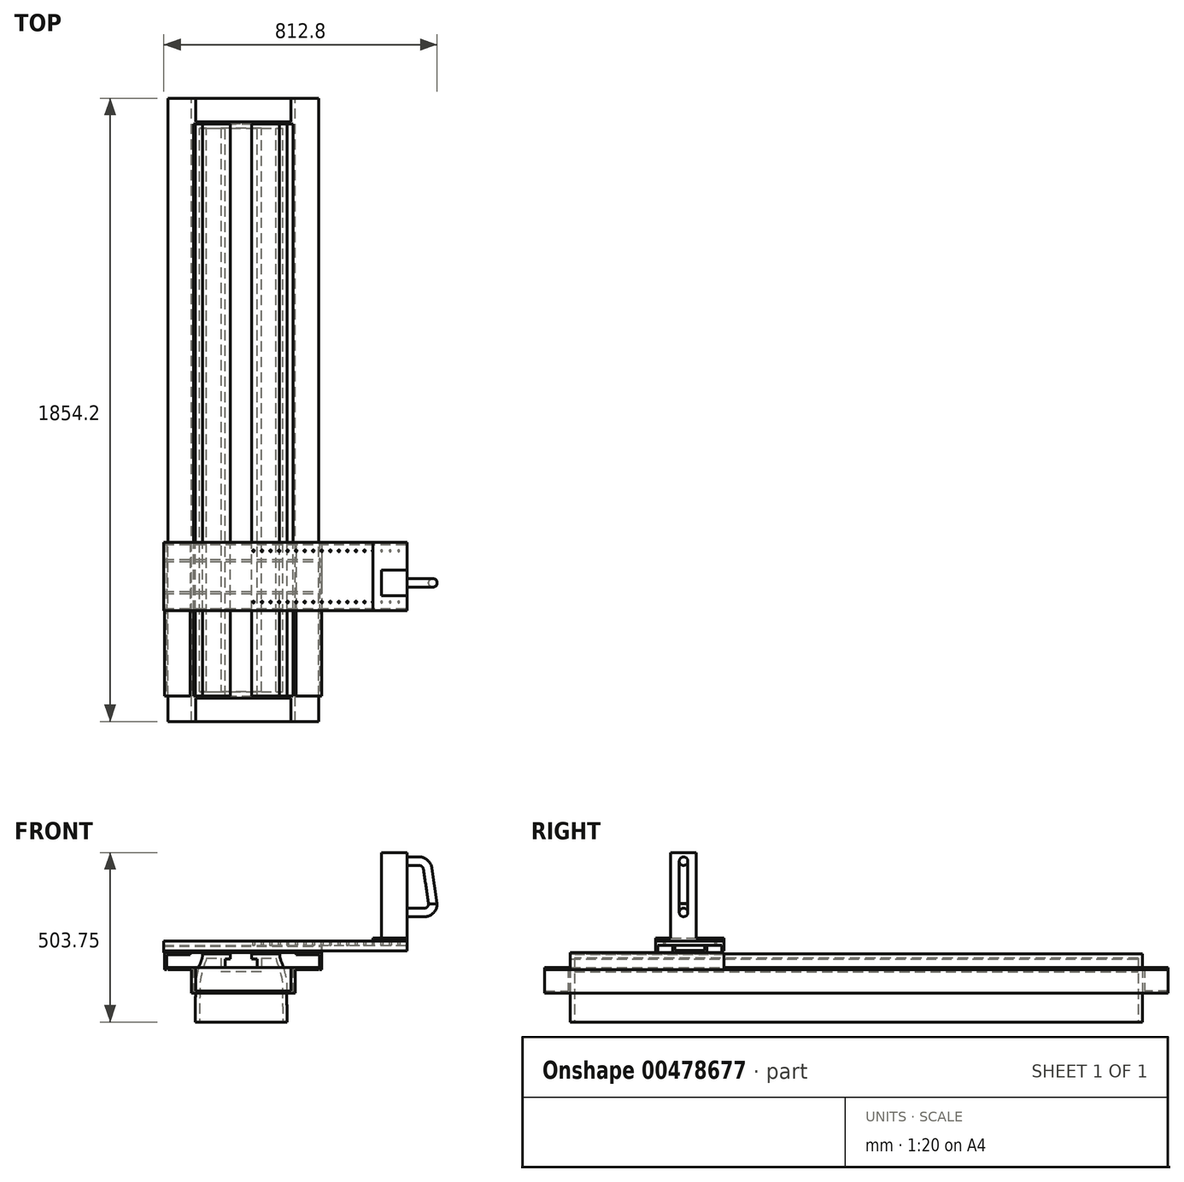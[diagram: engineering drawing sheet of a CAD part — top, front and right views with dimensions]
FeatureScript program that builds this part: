
annotation { "Feature Type Name" : "Feature", "Feature Type Description" : "" }
export const myFeature = defineFeature(function(context is Context, id is Id, definition is map)
    precondition{}
    {
        {
            var Q0;
            Q0=qCreatedBy(makeId("Front.planeOp"),FACE);
            var sketch = newSketch(context, id + "F0", { "sketchPlane" : qUnion([Q0])});
            skLineSegment(sketch, "E0.bottom", {"start": v(0, 0) * mm, "end": v(136.53, 0) * mm});
            skLineSegment(sketch, "E0.top", {"start": v(22.23, 203.2) * mm, "end": v(104.78, 203.2) * mm});
            skLineSegment(sketch, "E1.left", {"start": v(-15.88, 0) * mm, "end": v(-15.88, 203.2) * mm, "construction": true});
            skPoint(sketch, "E2", {"position": v(22.23, 203.2) * mm});
            skPoint(sketch, "E3", {"position": v(20.52, 190.5) * mm});
            skPoint(sketch, "E4", {"position": v(16.18, 177.8) * mm});
            skPoint(sketch, "E5", {"position": v(11.43, 165.1) * mm});
            skPoint(sketch, "E6", {"position": v(8.2, 152.4) * mm});
            skPoint(sketch, "E7", {"position": v(4.98, 139.7) * mm});
            skPoint(sketch, "E8", {"position": v(2.49, 127) * mm});
            skPoint(sketch, "E9", {"position": v(1.37, 114.3) * mm});
            skPoint(sketch, "E10", {"position": v(1.07, 101.6) * mm});
            skFitSpline(sketch, "E11", {"points": [v(22.23, 203.2) * mm, v(20.52, 190.5) * mm, v(16.18, 177.8) * mm, v(11.43, 165.1) * mm, v(8.2, 152.4) * mm, v(4.98, 139.7) * mm, v(2.49, 127) * mm, v(1.37, 114.3) * mm, v(1.07, 101.6) * mm, v(0, 0) * mm], "startDerivative": vector(-11.78, -139.04) * mm, "endDerivative": vector(-5, -490.08) * mm});
            skPoint(sketch, "E12", {"position": v(136.53, 0) * mm});
            skLineSegment(sketch, "E13", {"start": v(136.52, 203.2) * mm, "end": v(136.52, 0) * mm, "construction": true});
            skFitSpline(sketch, "E14.MirrorCS", {"points": [v(250.82, 203.2) * mm, v(252.53, 190.5) * mm, v(256.87, 177.8) * mm, v(261.62, 165.1) * mm, v(264.86, 152.4) * mm, v(268.07, 139.7) * mm, v(270.56, 127) * mm, v(271.68, 114.3) * mm, v(271.98, 101.6) * mm, v(273.05, 0) * mm], "startDerivative": vector(11.78, -139.04) * mm, "endDerivative": vector(5, -490.08) * mm});
            skLineSegment(sketch, "E15.MirrorCS", {"start": v(273.05, 0) * mm, "end": v(136.53, 0) * mm});
            skPoint(sketch, "E16.middle", {"position": v(136.52, 203.2) * mm});
            skLineSegment(sketch, "E17", {"start": v(104.78, 203.2) * mm, "end": v(104.78, 187.33) * mm});
            skLineSegment(sketch, "E18", {"start": v(104.78, 187.33) * mm, "end": v(88.9, 187.33) * mm});
            skLineSegment(sketch, "E19", {"start": v(88.9, 187.33) * mm, "end": v(88.9, 161.93) * mm});
            skLineSegment(sketch, "E20", {"start": v(88.9, 161.93) * mm, "end": v(136.52, 161.93) * mm});
            skLineSegment(sketch, "E21.MirrorCS", {"start": v(184.15, 187.33) * mm, "end": v(184.15, 161.93) * mm});
            skLineSegment(sketch, "E22.MirrorCS", {"start": v(184.15, 161.93) * mm, "end": v(136.53, 161.93) * mm});
            skLineSegment(sketch, "E23.MirrorCS", {"start": v(168.28, 187.33) * mm, "end": v(184.15, 187.33) * mm});
            skLineSegment(sketch, "E24.MirrorCS", {"start": v(168.28, 203.2) * mm, "end": v(168.28, 187.33) * mm});
            skPoint(sketch, "E25", {"position": v(104.78, 203.2) * mm});
            skPoint(sketch, "E26", {"position": v(168.28, 203.2) * mm});
            skLineSegment(sketch, "E27", {"start": v(168.28, 203.2) * mm, "end": v(250.83, 203.2) * mm});
            skLineSegment(sketch, "E28", {"start": v(0, 0) * mm, "end": v(2.5, 237.7) * mm, "construction": true});
            skSolve(sketch);
        }
        {
            var Q0;
            Q0=makeQuery(id+"F0.imprint","IMPRINT",FACE,{"disambiguationData":[TD([[makeQuery(id+"F0.imprint","IMPRINT",EDGE,{"derivedFrom":sQuery(id+"F0.wireOp",EDGE,"E0.bottom")}),1.0]])]});
            extrude(context, id + "F1", {"entities" : qUnion([Q0]), "depth" : 1701.8 * mm, "offsetDistance" : 25.4 * mm});
        }
        {
            var Q0;
            Q0=makeQuery(id+"F1.opExtrude","SWEPT_FACE",FACE,{"disambiguationData":[OSD([sQuery(id+"F0.wireOp",EDGE,"E0.bottom"),sQuery(id+"F0.wireOp",EDGE,"E15.MirrorCS")])]});
            shell(context, id + "F2", {"entities" : qUnion([Q0]), "thickness" : 12.7 * mm});
        }
        {
            var Q0;
            Q0=makeQuery(id+"F1.opExtrude","CAP_FACE",FACE,{"disambiguationData":[OSD([sQuery(id+"F0.wireOp",EDGE,"E0.bottom"),sQuery(id+"F0.wireOp",EDGE,"E0.top"),sQuery(id+"F0.wireOp",EDGE,"E11"),sQuery(id+"F0.wireOp",EDGE,"E14.MirrorCS"),sQuery(id+"F0.wireOp",EDGE,"E15.MirrorCS"),sQuery(id+"F0.wireOp",EDGE,"E17"),sQuery(id+"F0.wireOp",EDGE,"E18"),sQuery(id+"F0.wireOp",EDGE,"E19"),sQuery(id+"F0.wireOp",EDGE,"E20"),sQuery(id+"F0.wireOp",EDGE,"E21.MirrorCS"),sQuery(id+"F0.wireOp",EDGE,"E22.MirrorCS"),sQuery(id+"F0.wireOp",EDGE,"E23.MirrorCS"),sQuery(id+"F0.wireOp",EDGE,"E24.MirrorCS"),sQuery(id+"F0.wireOp",EDGE,"E27")])],"isStart":true});
            var sketch = newSketch(context, id + "F3", { "sketchPlane" : qUnion([Q0])});
            skLineSegment(sketch, "E29.bottom", {"start": v(-290.95, 85.73) * mm, "end": v(5.4, 85.73) * mm});
            skPoint(sketch, "E29.middle", {"position": v(-136.52, 123.83) * mm});
            skLineSegment(sketch, "E30", {"start": v(-284.6, 92.08) * mm, "end": v(-0.95, 92.08) * mm});
            skLineSegment(sketch, "E31", {"start": v(5.4, 161.93) * mm, "end": v(5.4, 85.73) * mm});
            skLineSegment(sketch, "E32.trimOffspring", {"start": v(-290.95, 161.92) * mm, "end": v(5.4, 161.93) * mm});
            skLineSegment(sketch, "E33", {"start": v(-290.95, 161.92) * mm, "end": v(-290.95, 85.73) * mm});
            skLineSegment(sketch, "E34", {"start": v(-0.95, 92.08) * mm, "end": v(-0.95, 161.93) * mm});
            skPoint(sketch, "E35.orphan", {"position": v(-0.95, 85.73) * mm});
            skLineSegment(sketch, "E36", {"start": v(-284.6, 161.92) * mm, "end": v(-284.6, 92.08) * mm});
            skSolve(sketch);
        }
        {
            var Q0;
            Q0 = qSketchRegion(id + "F3", true);
            extrude(context, id + "F4", {"entities" : qUnion([Q0]), "depth" : 6.35 * mm, "offsetDistance" : 25.4 * mm});
        }
        {
            var Q0;
            {var subQ4=sQuery(id+"F3.wireOp",EDGE,"E29.left");Q0=makeQuery(id+"F3.imprint","IMPRINT",FACE,{"disambiguationData":[TD([[makeQuery(id+"F3.imprint","IMPRINT",EDGE,{"derivedFrom":subQ4}),-1.0]])]});}
            var Q1;
            {var subQ0=sQuery(id+"F3.wireOp",EDGE,"E29.bottom");var subQ1=makeQuery(id+"F1.opExtrude","CAP_EDGE",EDGE,{"disambiguationData":[OSD([sQuery(id+"F0.wireOp",EDGE,"E14.MirrorCS")])],"isStart":true});var subQ2=makeQuery(id+"F3.imprint","INTERSECT",VERTEX,{"derivedFrom":[subQ1,subQ0]});Q1=makeQuery(id+"F3.imprint","IMPRINT",FACE,{"disambiguationData":[TD([[makeQuery(id+"F3.imprint","IMPRINT",EDGE,{"disambiguationData":[TD([[subQ2,-1.0]])],"derivedFrom":subQ0}),1.0]])]});}
            var Q2;
            {var subQ4=sQuery(id+"F3.wireOp",EDGE,"E29.right");Q2=makeQuery(id+"F3.imprint","IMPRINT",FACE,{"disambiguationData":[TD([[makeQuery(id+"F3.imprint","IMPRINT",EDGE,{"derivedFrom":subQ4}),1.0]])]});}
            extrude(context, id + "F5", {"entities" : qUnion([Q0, Q1, Q2]), "operationType" : NewBodyOperationType.ADD, "depth" : 76.2 * mm, "offsetDistance" : 25.4 * mm});
        }
        {
            var Q0;
            Q0=makeQuery(id+"F5.opExtrude","CAP_FACE",FACE,{"disambiguationData":[OSD([sQuery(id+"F3.wireOp",EDGE,"E29.bottom"),sQuery(id+"F3.wireOp",EDGE,"E29.left"),sQuery(id+"F3.wireOp",EDGE,"E29.right"),sQuery(id+"F3.wireOp",EDGE,"E30")])],"isStart":false});
            var sketch = newSketch(context, id + "F6", { "sketchPlane" : qUnion([Q0])});
            skLineSegment(sketch, "E37", {"start": v(-367.15, 161.92) * mm, "end": v(-290.95, 161.92) * mm});
            skLineSegment(sketch, "E38", {"start": v(-290.95, 161.92) * mm, "end": v(-290.95, 85.72) * mm});
            skLineSegment(sketch, "E39", {"start": v(-290.95, 85.72) * mm, "end": v(-297.3, 85.72) * mm});
            skLineSegment(sketch, "E40", {"start": v(-297.3, 85.72) * mm, "end": v(-297.3, 155.57) * mm});
            skLineSegment(sketch, "E41", {"start": v(-297.3, 155.57) * mm, "end": v(-367.15, 155.57) * mm});
            skLineSegment(sketch, "E42", {"start": v(-367.15, 155.57) * mm, "end": v(-367.15, 161.92) * mm});
            skLineSegment(sketch, "E43", {"start": v(5.4, 85.73) * mm, "end": v(5.4, 161.93) * mm});
            skLineSegment(sketch, "E44", {"start": v(5.4, 161.93) * mm, "end": v(81.6, 161.93) * mm});
            skLineSegment(sketch, "E45", {"start": v(81.6, 161.93) * mm, "end": v(81.6, 155.58) * mm});
            skLineSegment(sketch, "E46", {"start": v(81.6, 155.58) * mm, "end": v(11.75, 155.58) * mm});
            skLineSegment(sketch, "E47", {"start": v(11.75, 155.58) * mm, "end": v(11.75, 85.73) * mm});
            skLineSegment(sketch, "E48", {"start": v(11.75, 85.73) * mm, "end": v(5.4, 85.73) * mm});
            skSolve(sketch);
        }
        {
            var Q0;
            Q0 = qSketchRegion(id + "F6", true);
            extrude(context, id + "F7", {"entities" : qUnion([Q0]), "oppositeDirection" : true, "depth" : 1854.2 * mm, "offsetDistance" : 25.4 * mm});
        }
        {
            var Q0;
            {var subQ0=sQuery(id+"F3.wireOp",EDGE,"E33");Q0=makeQuery(id+"F3.imprint","IMPRINT",FACE,{"disambiguationData":[TD([[makeQuery(id+"F3.imprint","IMPRINT",EDGE,{"derivedFrom":subQ0}),1.0]])]});}
            var Q1;
            {var subQ0=sQuery(id+"F3.wireOp",EDGE,"E31");Q1=makeQuery(id+"F3.imprint","IMPRINT",FACE,{"disambiguationData":[TD([[makeQuery(id+"F3.imprint","IMPRINT",EDGE,{"derivedFrom":subQ0}),-1.0]])]});}
            extrude(context, id + "F8", {"entities" : qUnion([Q0, Q1]), "operationType" : NewBodyOperationType.ADD, "depth" : 76.2 * mm, "offsetDistance" : 25.4 * mm});
        }
        {
            var Q0;
            Q0=makeQuery(id+"F1.opExtrude","CAP_FACE",FACE,{"disambiguationData":[OSD([sQuery(id+"F0.wireOp",EDGE,"E0.bottom"),sQuery(id+"F0.wireOp",EDGE,"E0.top"),sQuery(id+"F0.wireOp",EDGE,"E11"),sQuery(id+"F0.wireOp",EDGE,"E14.MirrorCS"),sQuery(id+"F0.wireOp",EDGE,"E15.MirrorCS"),sQuery(id+"F0.wireOp",EDGE,"E17"),sQuery(id+"F0.wireOp",EDGE,"E18"),sQuery(id+"F0.wireOp",EDGE,"E19"),sQuery(id+"F0.wireOp",EDGE,"E20"),sQuery(id+"F0.wireOp",EDGE,"E21.MirrorCS"),sQuery(id+"F0.wireOp",EDGE,"E22.MirrorCS"),sQuery(id+"F0.wireOp",EDGE,"E23.MirrorCS"),sQuery(id+"F0.wireOp",EDGE,"E24.MirrorCS"),sQuery(id+"F0.wireOp",EDGE,"E27")])],"isStart":false});
            var sketch = newSketch(context, id + "F9", { "sketchPlane" : qUnion([Q0])});
            skLineSegment(sketch, "E49.bottom", {"start": v(-5.4, 85.73) * mm, "end": v(290.95, 85.73) * mm});
            skLineSegment(sketch, "E49.top", {"start": v(-5.4, 161.92) * mm, "end": v(290.95, 161.92) * mm});
            skLineSegment(sketch, "E49.left", {"start": v(-5.4, 85.33) * mm, "end": v(-5.4, 91.68) * mm});
            skLineSegment(sketch, "E49.right", {"start": v(290.95, 85.33) * mm, "end": v(290.95, 91.68) * mm});
            skLineSegment(sketch, "E50", {"start": v(-5.4, 161.92) * mm, "end": v(-5.4, 91.68) * mm});
            skLineSegment(sketch, "E51", {"start": v(290.95, 161.92) * mm, "end": v(290.95, 91.68) * mm});
            skLineSegment(sketch, "E52", {"start": v(0.95, 92.08) * mm, "end": v(284.6, 92.08) * mm});
            skLineSegment(sketch, "E53", {"start": v(0.95, 161.92) * mm, "end": v(0.95, 92.08) * mm});
            skLineSegment(sketch, "E54", {"start": v(284.6, 161.92) * mm, "end": v(284.6, 92.08) * mm});
            skSolve(sketch);
        }
        {
            var Q0;
            {var subQ0=sQuery(id+"F9.wireOp",EDGE,"E49.top");var subQ1=makeQuery(id+"F1.opExtrude","CAP_EDGE",EDGE,{"disambiguationData":[OSD([sQuery(id+"F0.wireOp",EDGE,"E11")])],"isStart":false});var subQ2=makeQuery(id+"F9.imprint","INTERSECT",VERTEX,{"derivedFrom":[subQ1,subQ0]});Q0=makeQuery(id+"F9.imprint","IMPRINT",FACE,{"disambiguationData":[TD([[makeQuery(id+"F9.imprint","IMPRINT",EDGE,{"disambiguationData":[TD([[subQ2,-1.0]])],"derivedFrom":subQ0}),-1.0]])]});}
            var Q1;
            {var subQ0=sQuery(id+"F9.wireOp",EDGE,"E54");Q1=makeQuery(id+"F9.imprint","IMPRINT",FACE,{"disambiguationData":[TD([[makeQuery(id+"F9.imprint","IMPRINT",EDGE,{"derivedFrom":subQ0}),-1.0]])]});}
            var Q2;
            {var subQ0=sQuery(id+"F9.wireOp",EDGE,"E53");Q2=makeQuery(id+"F9.imprint","IMPRINT",FACE,{"disambiguationData":[TD([[makeQuery(id+"F9.imprint","IMPRINT",EDGE,{"derivedFrom":subQ0}),1.0]])]});}
            extrude(context, id + "F10", {"entities" : qUnion([Q0, Q1, Q2]), "depth" : 6.35 * mm, "offsetDistance" : 25.4 * mm});
        }
        {
            var Q0;
            {var subQ5=sQuery(id+"F9.wireOp",EDGE,"E49.right");Q0=makeQuery(id+"F9.imprint","IMPRINT",FACE,{"disambiguationData":[TD([[makeQuery(id+"F9.imprint","IMPRINT",EDGE,{"derivedFrom":subQ5}),1.0]])]});}
            var Q1;
            {var subQ0=sQuery(id+"F9.wireOp",EDGE,"E49.bottom");var subQ1=makeQuery(id+"F1.opExtrude","CAP_EDGE",EDGE,{"disambiguationData":[OSD([sQuery(id+"F0.wireOp",EDGE,"E11")])],"isStart":false});var subQ2=makeQuery(id+"F9.imprint","INTERSECT",VERTEX,{"derivedFrom":[subQ1,subQ0]});Q1=makeQuery(id+"F9.imprint","IMPRINT",FACE,{"disambiguationData":[TD([[makeQuery(id+"F9.imprint","IMPRINT",EDGE,{"disambiguationData":[TD([[subQ2,-1.0]])],"derivedFrom":subQ0}),1.0]])]});}
            var Q2;
            {var subQ0=sQuery(id+"F9.wireOp",EDGE,"E51");Q2=makeQuery(id+"F9.imprint","IMPRINT",FACE,{"disambiguationData":[TD([[makeQuery(id+"F9.imprint","IMPRINT",EDGE,{"derivedFrom":subQ0}),-1.0]])]});}
            var Q3;
            {var subQ0=sQuery(id+"F9.wireOp",EDGE,"E50");Q3=makeQuery(id+"F9.imprint","IMPRINT",FACE,{"disambiguationData":[TD([[makeQuery(id+"F9.imprint","IMPRINT",EDGE,{"derivedFrom":subQ0}),1.0]])]});}
            extrude(context, id + "F11", {"entities" : qUnion([Q0, Q1, Q2, Q3]), "operationType" : NewBodyOperationType.ADD, "depth" : 76.2 * mm, "offsetDistance" : 25.4 * mm});
        }
        {
            var Q0;
            {var subQ0=makeQuery(id+"F1.opExtrude","CAP_EDGE",EDGE,{"disambiguationData":[OSD([sQuery(id+"F0.wireOp",EDGE,"E0.top")])],"isStart":false});Q0=makeQuery(id+"F9.imprint","IMPRINT",FACE,{"disambiguationData":[TD([[makeQuery(id+"F9.imprint","IMPRINT",EDGE,{"derivedFrom":subQ0}),-1.0]])]});}
            var sketch = newSketch(context, id + "F12", { "sketchPlane" : qUnion([Q0])});
            skLineSegment(sketch, "E55", {"start": v(-91.12, 155.57) * mm, "end": v(-91.12, 206.37) * mm});
            skLineSegment(sketch, "E56", {"start": v(-91.12, 206.37) * mm, "end": v(-14.92, 206.37) * mm});
            skLineSegment(sketch, "E57", {"start": v(-14.92, 206.37) * mm, "end": v(-14.92, 200.02) * mm});
            skLineSegment(sketch, "E58", {"start": v(-14.92, 200.02) * mm, "end": v(-84.77, 200.02) * mm});
            skLineSegment(sketch, "E59", {"start": v(-84.77, 200.02) * mm, "end": v(-84.77, 155.57) * mm});
            skLineSegment(sketch, "E60", {"start": v(-84.77, 155.57) * mm, "end": v(-91.12, 155.57) * mm});
            skLineSegment(sketch, "E61", {"start": v(300.48, 206.37) * mm, "end": v(376.68, 206.37) * mm});
            skLineSegment(sketch, "E62", {"start": v(376.68, 206.37) * mm, "end": v(376.68, 155.57) * mm});
            skLineSegment(sketch, "E63", {"start": v(376.68, 155.57) * mm, "end": v(370.33, 155.57) * mm});
            skLineSegment(sketch, "E64", {"start": v(370.33, 155.57) * mm, "end": v(370.33, 200.02) * mm});
            skLineSegment(sketch, "E65", {"start": v(370.33, 200.02) * mm, "end": v(300.48, 200.02) * mm});
            skLineSegment(sketch, "E66", {"start": v(300.48, 200.02) * mm, "end": v(300.48, 206.37) * mm});
            skSolve(sketch);
        }
        {
            var Q0;
            Q0 = qSketchRegion(id + "F12", true);
            extrude(context, id + "F13", {"entities" : qUnion([Q0]), "oppositeDirection" : true, "depth" : 457.2 * mm, "offsetDistance" : 25.4 * mm});
        }
        {
            var Q0;
            Q0=makeQuery(id+"F13.opExtrude","SWEPT_FACE",FACE,{"disambiguationData":[OSD([sQuery(id+"F12.wireOp",EDGE,"E62")])]});
            var sketch = newSketch(context, id + "F14", { "sketchPlane" : qUnion([Q0])});
            skLineSegment(sketch, "E67.bottom", {"start": v(-1397, 206.37) * mm, "end": v(-1295.4, 206.37) * mm});
            skLineSegment(sketch, "E67.top", {"start": v(-1397, 225.42) * mm, "end": v(-1390.65, 225.42) * mm});
            skLineSegment(sketch, "E67.left", {"start": v(-1397, 206.37) * mm, "end": v(-1397, 225.42) * mm});
            skLineSegment(sketch, "E67.right", {"start": v(-1295.4, 206.37) * mm, "end": v(-1295.4, 225.42) * mm});
            skLineSegment(sketch, "E68.top", {"start": v(-1390.65, 212.72) * mm, "end": v(-1301.75, 212.72) * mm});
            skLineSegment(sketch, "E68.left", {"start": v(-1390.65, 225.42) * mm, "end": v(-1390.65, 212.72) * mm});
            skLineSegment(sketch, "E68.right", {"start": v(-1301.75, 225.42) * mm, "end": v(-1301.75, 212.72) * mm});
            skLineSegment(sketch, "E69.trimOffspring", {"start": v(-1301.75, 225.42) * mm, "end": v(-1295.4, 225.42) * mm});
            skSolve(sketch);
        }
        {
            var Q0;
            Q0 = qSketchRegion(id + "F14", true);
            extrude(context, id + "F15", {"entities" : qUnion([Q0]), "oppositeDirection" : true, "depth" : 469.9 * mm, "offsetDistance" : 25.4 * mm});
        }
        {
            var Q0;
            Q0=makeQuery(id+"F13.opExtrude","SWEPT_FACE",FACE,{"disambiguationData":[OSD([sQuery(id+"F12.wireOp",EDGE,"E62")])]});
            var sketch = newSketch(context, id + "F16", { "sketchPlane" : qUnion([Q0])});
            skLineSegment(sketch, "E70.top", {"start": v(-1244.6, 240.22) * mm, "end": v(-1447.8, 240.22) * mm});
            skLineSegment(sketch, "E71", {"start": v(-1447.8, 240.22) * mm, "end": v(-1447.8, 211.65) * mm});
            skLineSegment(sketch, "E72", {"start": v(-1447.8, 211.65) * mm, "end": v(-1441.45, 211.65) * mm});
            skLineSegment(sketch, "E73", {"start": v(-1441.45, 211.65) * mm, "end": v(-1441.45, 227.52) * mm});
            skLineSegment(sketch, "E74", {"start": v(-1441.45, 227.52) * mm, "end": v(-1250.95, 227.52) * mm});
            skLineSegment(sketch, "E75", {"start": v(-1250.95, 227.52) * mm, "end": v(-1250.95, 211.65) * mm});
            skLineSegment(sketch, "E76", {"start": v(-1250.95, 211.65) * mm, "end": v(-1244.6, 211.65) * mm});
            skLineSegment(sketch, "E77", {"start": v(-1244.6, 211.65) * mm, "end": v(-1244.6, 240.22) * mm});
            skSolve(sketch);
        }
        {
            var Q0;
            Q0 = qSketchRegion(id + "F16", true);
            extrude(context, id + "F17", {"entities" : qUnion([Q0]), "oppositeDirection" : true, "depth" : 469.9 * mm, "offsetDistance" : 25.4 * mm, "hasSecondDirection" : true, "secondDirectionOppositeDirection" : false, "secondDirectionDepth" : 254 * mm});
        }
        {
            var Q0;
            Q0=makeQuery(id+"F17.opExtrude","SWEPT_FACE",FACE,{"disambiguationData":[OSD([sQuery(id+"F16.wireOp",EDGE,"E70.top")])]});
            var sketch = newSketch(context, id + "F18", { "sketchPlane" : qUnion([Q0])});
            skPoint(sketch, "E78", {"position": v(605.28, -1270) * mm});
            skPoint(sketch, "E79", {"position": v(605.28, -1422.4) * mm});
            skPoint(sketch, "E80.1.0.0", {"position": v(579.88, -1270) * mm});
            skPoint(sketch, "E80.1.0.1", {"position": v(579.88, -1422.4) * mm});
            skPoint(sketch, "E80.2.0.0", {"position": v(554.48, -1270) * mm});
            skPoint(sketch, "E80.2.0.1", {"position": v(554.48, -1422.4) * mm});
            skPoint(sketch, "E80.3.0.0", {"position": v(529.08, -1270) * mm});
            skPoint(sketch, "E80.3.0.1", {"position": v(529.08, -1422.4) * mm});
            skPoint(sketch, "E80.4.0.0", {"position": v(503.68, -1270) * mm});
            skPoint(sketch, "E80.4.0.1", {"position": v(503.68, -1422.4) * mm});
            skPoint(sketch, "E80.5.0.0", {"position": v(478.28, -1270) * mm});
            skPoint(sketch, "E80.5.0.1", {"position": v(478.28, -1422.4) * mm});
            skPoint(sketch, "E80.6.0.0", {"position": v(452.88, -1270) * mm});
            skPoint(sketch, "E80.6.0.1", {"position": v(452.88, -1422.4) * mm});
            skPoint(sketch, "E80.7.0.0", {"position": v(427.48, -1270) * mm});
            skPoint(sketch, "E80.7.0.1", {"position": v(427.48, -1422.4) * mm});
            skPoint(sketch, "E80.8.0.0", {"position": v(402.08, -1270) * mm});
            skPoint(sketch, "E80.8.0.1", {"position": v(402.08, -1422.4) * mm});
            skPoint(sketch, "E80.9.0.0", {"position": v(376.68, -1270) * mm});
            skPoint(sketch, "E80.9.0.1", {"position": v(376.68, -1422.4) * mm});
            skPoint(sketch, "E80.10.0.0", {"position": v(351.28, -1270) * mm});
            skPoint(sketch, "E80.10.0.1", {"position": v(351.28, -1422.4) * mm});
            skPoint(sketch, "E80.11.0.0", {"position": v(325.88, -1270) * mm});
            skPoint(sketch, "E80.11.0.1", {"position": v(325.88, -1422.4) * mm});
            skPoint(sketch, "E80.12.0.0", {"position": v(300.48, -1270) * mm});
            skPoint(sketch, "E80.12.0.1", {"position": v(300.48, -1422.4) * mm});
            skPoint(sketch, "E80.13.0.0", {"position": v(275.08, -1270) * mm});
            skPoint(sketch, "E80.13.0.1", {"position": v(275.08, -1422.4) * mm});
            skPoint(sketch, "E80.14.0.0", {"position": v(249.68, -1270) * mm});
            skPoint(sketch, "E80.14.0.1", {"position": v(249.68, -1422.4) * mm});
            skPoint(sketch, "E80.15.0.0", {"position": v(224.28, -1270) * mm});
            skPoint(sketch, "E80.15.0.1", {"position": v(224.28, -1422.4) * mm});
            skPoint(sketch, "E80.16.0.0", {"position": v(198.88, -1270) * mm});
            skPoint(sketch, "E80.16.0.1", {"position": v(198.88, -1422.4) * mm});
            skPoint(sketch, "E80.17.0.0", {"position": v(173.48, -1270) * mm});
            skPoint(sketch, "E80.17.0.1", {"position": v(173.48, -1422.4) * mm});
            skLineSegment(sketch, "E80.direction1", {"start": v(605.28, -1270) * mm, "end": v(579.88, -1270) * mm, "construction": true});
            skSolve(sketch);
        }
        {
            var Q0;
            Q0=sQuery(id+"F18.wireOp",VERTEX,"E78");
            var Q1;
            Q1=sQuery(id+"F18.wireOp",VERTEX,"E80.1.0.0");
            var Q2;
            Q2=sQuery(id+"F18.wireOp",VERTEX,"E80.2.0.0");
            var Q3;
            Q3=sQuery(id+"F18.wireOp",VERTEX,"E80.3.0.0");
            var Q4;
            Q4=sQuery(id+"F18.wireOp",VERTEX,"E80.4.0.0");
            var Q5;
            Q5=sQuery(id+"F18.wireOp",VERTEX,"E80.5.0.0");
            var Q6;
            Q6=sQuery(id+"F18.wireOp",VERTEX,"E80.6.0.0");
            var Q7;
            Q7=sQuery(id+"F18.wireOp",VERTEX,"E80.7.0.0");
            var Q8;
            Q8=sQuery(id+"F18.wireOp",VERTEX,"E80.8.0.0");
            var Q9;
            Q9=sQuery(id+"F18.wireOp",VERTEX,"E80.9.0.0");
            var Q10;
            Q10=sQuery(id+"F18.wireOp",VERTEX,"E80.10.0.0");
            var Q11;
            Q11=sQuery(id+"F18.wireOp",VERTEX,"E80.11.0.0");
            var Q12;
            Q12=sQuery(id+"F18.wireOp",VERTEX,"E80.12.0.0");
            var Q13;
            Q13=sQuery(id+"F18.wireOp",VERTEX,"E80.13.0.0");
            var Q14;
            Q14=sQuery(id+"F18.wireOp",VERTEX,"E80.14.0.0");
            var Q15;
            Q15=sQuery(id+"F18.wireOp",VERTEX,"E80.15.0.0");
            var Q16;
            Q16=sQuery(id+"F18.wireOp",VERTEX,"E80.16.0.0");
            var Q17;
            Q17=sQuery(id+"F18.wireOp",VERTEX,"E80.17.0.0");
            var Q18;
            Q18=sQuery(id+"F18.wireOp",VERTEX,"E79");
            var Q19;
            Q19=sQuery(id+"F18.wireOp",VERTEX,"E80.1.0.1");
            var Q20;
            Q20=sQuery(id+"F18.wireOp",VERTEX,"E80.2.0.1");
            var Q21;
            Q21=sQuery(id+"F18.wireOp",VERTEX,"E80.3.0.1");
            var Q22;
            Q22=sQuery(id+"F18.wireOp",VERTEX,"E80.4.0.1");
            var Q23;
            Q23=sQuery(id+"F18.wireOp",VERTEX,"E80.5.0.1");
            var Q24;
            Q24=sQuery(id+"F18.wireOp",VERTEX,"E80.6.0.1");
            var Q25;
            Q25=sQuery(id+"F18.wireOp",VERTEX,"E80.7.0.1");
            var Q26;
            Q26=sQuery(id+"F18.wireOp",VERTEX,"E80.8.0.1");
            var Q27;
            Q27=sQuery(id+"F18.wireOp",VERTEX,"E80.9.0.1");
            var Q28;
            Q28=sQuery(id+"F18.wireOp",VERTEX,"E80.10.0.1");
            var Q29;
            Q29=sQuery(id+"F18.wireOp",VERTEX,"E80.11.0.1");
            var Q30;
            Q30=sQuery(id+"F18.wireOp",VERTEX,"E80.12.0.1");
            var Q31;
            Q31=sQuery(id+"F18.wireOp",VERTEX,"E80.13.0.1");
            var Q32;
            Q32=sQuery(id+"F18.wireOp",VERTEX,"E80.14.0.1");
            var Q33;
            Q33=sQuery(id+"F18.wireOp",VERTEX,"E80.15.0.1");
            var Q34;
            Q34=sQuery(id+"F18.wireOp",VERTEX,"E80.16.0.1");
            var Q35;
            Q35=sQuery(id+"F18.wireOp",VERTEX,"E80.17.0.1");
            var Q36;
            Q36=makeQuery(id+"F1.opExtrude","SWEPT_BODY",BODY,{"disambiguationData":[OSD([sQuery(id+"F0.wireOp",EDGE,"E0.bottom"),sQuery(id+"F0.wireOp",EDGE,"E0.top"),sQuery(id+"F0.wireOp",EDGE,"E11"),sQuery(id+"F0.wireOp",EDGE,"E14.MirrorCS"),sQuery(id+"F0.wireOp",EDGE,"E15.MirrorCS"),sQuery(id+"F0.wireOp",EDGE,"E17"),sQuery(id+"F0.wireOp",EDGE,"E18"),sQuery(id+"F0.wireOp",EDGE,"E19"),sQuery(id+"F0.wireOp",EDGE,"E20"),sQuery(id+"F0.wireOp",EDGE,"E21.MirrorCS"),sQuery(id+"F0.wireOp",EDGE,"E22.MirrorCS"),sQuery(id+"F0.wireOp",EDGE,"E23.MirrorCS"),sQuery(id+"F0.wireOp",EDGE,"E24.MirrorCS"),sQuery(id+"F0.wireOp",EDGE,"E27")])]});
            var Q37;
            Q37=makeQuery(id+"F7.opExtrude","SWEPT_BODY",BODY,{"disambiguationData":[OSD([sQuery(id+"F6.wireOp",EDGE,"E37"),sQuery(id+"F6.wireOp",EDGE,"E38"),sQuery(id+"F6.wireOp",EDGE,"E39"),sQuery(id+"F6.wireOp",EDGE,"E40"),sQuery(id+"F6.wireOp",EDGE,"E41"),sQuery(id+"F6.wireOp",EDGE,"E42")])]});
            var Q38;
            Q38=makeQuery(id+"F13.opExtrude","SWEPT_BODY",BODY,{"disambiguationData":[OSD([sQuery(id+"F12.wireOp",EDGE,"E61"),sQuery(id+"F12.wireOp",EDGE,"E62"),sQuery(id+"F12.wireOp",EDGE,"E63"),sQuery(id+"F12.wireOp",EDGE,"E64"),sQuery(id+"F12.wireOp",EDGE,"E65"),sQuery(id+"F12.wireOp",EDGE,"E66")])]});
            var Q39;
            Q39=makeQuery(id+"F17.opExtrude","SWEPT_BODY",BODY,{"disambiguationData":[OSD([sQuery(id+"F16.wireOp",EDGE,"E70.top"),sQuery(id+"F16.wireOp",EDGE,"E71"),sQuery(id+"F16.wireOp",EDGE,"E72"),sQuery(id+"F16.wireOp",EDGE,"E73"),sQuery(id+"F16.wireOp",EDGE,"E74"),sQuery(id+"F16.wireOp",EDGE,"E75"),sQuery(id+"F16.wireOp",EDGE,"E76"),sQuery(id+"F16.wireOp",EDGE,"E77")])]});
            hole(context, id + "F19", {"style" : HoleStyle.SIMPLE, "endStyle" : HoleEndStyle.BLIND, "standardTappedOrClearance" : lookupTablePath({ "standard" : "ANSI", "engagement" : "75%", "pitch" : "20 tpi", "size" : "1/4", "type" : "Tapped" }), "standardBlindInLast" : lookupTablePath({ "standard" : "ANSI", "fit" : "Normal", "engagement" : "75%", "pitch" : "20 tpi", "size" : "1/4", "type" : "Clearance & tapped" }), "holeDiameter" : 5.1 * mm, "majorDiameter" : 6.35 * mm, "showTappedDepth" : true, "holeDepth" : 19.68 * mm, "tappedDepth" : 15.88 * mm, "tapClearance" : 3, "startFromSketch" : true, "locations" : qUnion([Q0, Q1, Q2, Q3, Q4, Q5, Q6, Q7, Q8, Q9, Q10, Q11, Q12, Q13, Q14, Q15, Q16, Q17, Q18, Q19, Q20, Q21, Q22, Q23, Q24, Q25, Q26, Q27, Q28, Q29, Q30, Q31, Q32, Q33, Q34, Q35]), "scope" : qUnion([Q36, Q37, Q38, Q39])});
        }
        {
            var Q0;
            Q0=makeQuery(id+"F17.opExtrude","SWEPT_FACE",FACE,{"disambiguationData":[OSD([sQuery(id+"F16.wireOp",EDGE,"E70.top")])]});
            var sketch = newSketch(context, id + "F20", { "sketchPlane" : qUnion([Q0])});
            skLineSegment(sketch, "E81.bottom", {"start": v(630.68, -1447.8) * mm, "end": v(529.08, -1447.8) * mm});
            skLineSegment(sketch, "E81.top", {"start": v(630.68, -1244.6) * mm, "end": v(529.08, -1244.6) * mm});
            skLineSegment(sketch, "E81.left", {"start": v(630.68, -1447.8) * mm, "end": v(630.68, -1244.6) * mm});
            skLineSegment(sketch, "E81.right", {"start": v(529.08, -1447.8) * mm, "end": v(529.08, -1244.6) * mm});
            skSolve(sketch);
        }
        {
            var Q0;
            Q0 = qSketchRegion(id + "F20", true);
            extrude(context, id + "F21", {"entities" : qUnion([Q0]), "depth" : 9.52 * mm, "offsetDistance" : 25.4 * mm});
        }
        {
            var Q0;
            Q0=makeQuery(id+"F21.opExtrude","CAP_FACE",FACE,{"disambiguationData":[OSD([sQuery(id+"F20.wireOp",EDGE,"E81.bottom"),sQuery(id+"F20.wireOp",EDGE,"E81.top"),sQuery(id+"F20.wireOp",EDGE,"E81.left"),sQuery(id+"F20.wireOp",EDGE,"E81.right")])],"isStart":false});
            var sketch = newSketch(context, id + "F22", { "sketchPlane" : qUnion([Q0])});
            skLineSegment(sketch, "E82.bottom", {"start": v(630.68, -1403.35) * mm, "end": v(554.48, -1403.35) * mm});
            skLineSegment(sketch, "E82.top", {"start": v(630.68, -1327.15) * mm, "end": v(554.48, -1327.15) * mm});
            skLineSegment(sketch, "E82.left", {"start": v(630.68, -1403.35) * mm, "end": v(630.68, -1327.15) * mm});
            skLineSegment(sketch, "E82.right", {"start": v(554.48, -1403.35) * mm, "end": v(554.48, -1327.15) * mm});
            skSolve(sketch);
        }
        {
            var Q0;
            Q0 = qSketchRegion(id + "F22", true);
            extrude(context, id + "F23", {"entities" : qUnion([Q0]), "operationType" : NewBodyOperationType.ADD, "depth" : 254 * mm, "offsetDistance" : 25.4 * mm});
        }
        {
            var Q0;
            Q0=makeQuery(id+"F23.opExtrude","SWEPT_FACE",FACE,{"disambiguationData":[OSD([sQuery(id+"F22.wireOp",EDGE,"E82.bottom")])]});
            cPlane(context, id + "F24", {"entities" : qUnion([Q0]), "cplaneType" : CPlaneType.OFFSET, "offset" : 38.1 * mm, "oppositeDirection" : true, "width" : 152.4 * mm, "height" : 152.4 * mm});
        }
        {
            var Q0;
            Q0=qCreatedBy(id+"F24.planeOp",FACE);
            var sketch = newSketch(context, id + "F25", { "sketchPlane" : qUnion([Q0])});
            skLineSegment(sketch, "E83.top", {"start": v(630.68, 325.95) * mm, "end": v(681.48, 325.95) * mm});
            skLineSegment(sketch, "E83.left", {"start": v(630.68, 478.35) * mm, "end": v(630.68, 325.95) * mm});
            skPoint(sketch, "E84.visualSharp", {"position": v(687.83, 478.35) * mm});
            skPoint(sketch, "E85.visualSharp", {"position": v(706.88, 325.95) * mm});
            skArc(sketch, "E85.filletArc", {"start": v(681.48, 325.95) * mm, "mid": v(699.44, 333.39) * mm, "end": v(706.88, 351.35) * mm});
            skLineSegment(sketch, "E86", {"start": v(706.88, 351.35) * mm, "end": v(691.07, 456.72) * mm});
            skLineSegment(sketch, "E87", {"start": v(630.68, 478.35) * mm, "end": v(665.95, 478.35) * mm});
            skArc(sketch, "E88.filletArc", {"start": v(691.07, 456.72) * mm, "mid": v(682.53, 472.2) * mm, "end": v(665.95, 478.35) * mm});
            skSolve(sketch);
        }
        {
            var Q0;
            Q0=makeQuery(id+"F23.boolean.opBoolean","MERGE",FACE,{"derivedFrom":[makeQuery(id+"F21.opExtrude","SWEPT_FACE",FACE,{"disambiguationData":[OSD([sQuery(id+"F20.wireOp",EDGE,"E81.left")])]}),makeQuery(id+"F23.opExtrude","SWEPT_FACE",FACE,{"disambiguationData":[OSD([sQuery(id+"F22.wireOp",EDGE,"E82.left")])]})]});
            var sketch = newSketch(context, id + "F26", { "sketchPlane" : qUnion([Q0])});
            skCircle(sketch, "E89", {"center": v(-1365.25, 478.35) * mm, "radius": 12.7 * mm});
            skSolve(sketch);
        }
        {
            var Q0;
            Q0=makeQuery(id+"F26.imprint","IMPRINT",FACE,{"disambiguationData":[TD([[makeQuery(id+"F26.imprint","IMPRINT",EDGE,{"derivedFrom":sQuery(id+"F26.wireOp",EDGE,"E89")}),1.0]])]});
            var Q1;
            Q1=sQuery(id+"F25.wireOp",EDGE,"E87");
            var Q2;
            Q2=sQuery(id+"F25.wireOp",EDGE,"E88.filletArc");
            var Q3;
            Q3=sQuery(id+"F25.wireOp",EDGE,"E86");
            var Q4;
            Q4=sQuery(id+"F25.wireOp",EDGE,"E85.filletArc");
            var Q5;
            Q5=sQuery(id+"F25.wireOp",EDGE,"E83.top");
            sweep(context, id + "F27", {"operationType" : NewBodyOperationType.ADD, "profiles" : qUnion([Q0]), "path" : qUnion([Q1, Q2, Q3, Q4, Q5])});
        }
    });
